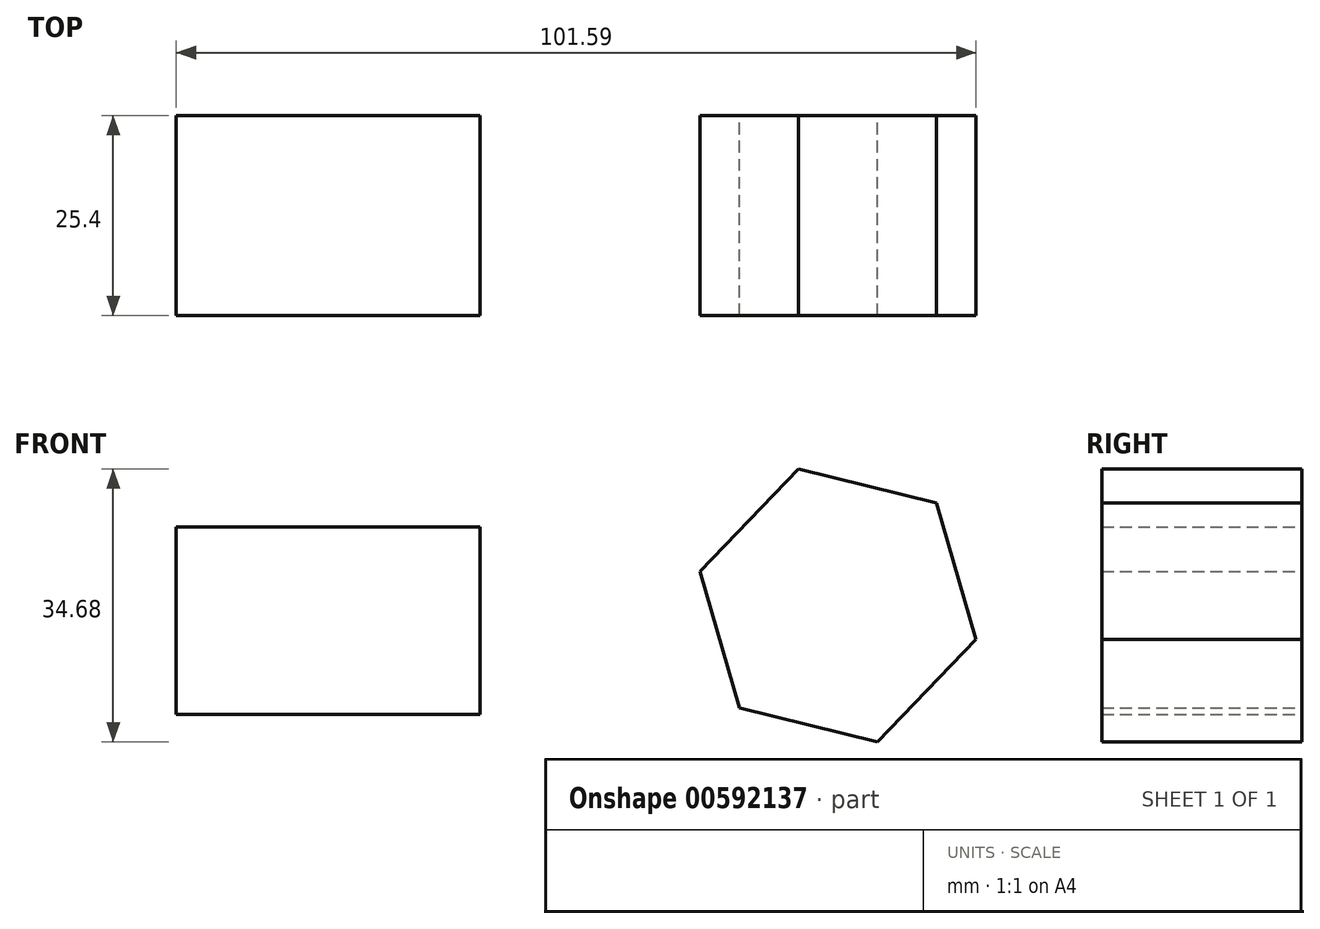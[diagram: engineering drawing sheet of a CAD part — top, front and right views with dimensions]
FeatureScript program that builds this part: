
annotation { "Feature Type Name" : "Feature", "Feature Type Description" : "" }
export const myFeature = defineFeature(function(context is Context, id is Id, definition is map)
    precondition{}
    {
        {
            var Q0;
            Q0=qCreatedBy(makeId("Front.planeOp"),FACE);
            var sketch = newSketch(context, id + "F0", { "sketchPlane" : qUnion([Q0])});
            skLineSegment(sketch, "E0.bottom", {"start": v(-62.62, 49.19) * mm, "end": v(-24.05, 49.19) * mm});
            skLineSegment(sketch, "E0.top", {"start": v(-62.62, 25.35) * mm, "end": v(-24.05, 25.35) * mm});
            skLineSegment(sketch, "E0.left", {"start": v(-62.62, 49.19) * mm, "end": v(-62.62, 25.35) * mm});
            skLineSegment(sketch, "E0.right", {"start": v(-24.05, 49.19) * mm, "end": v(-24.05, 25.35) * mm});
            skSolve(sketch);
        }
        {
            var Q0;
            Q0 = qSketchRegion(id + "F0", true);
            extrude(context, id + "F1", {"entities" : qUnion([Q0]), "depth" : 25.4 * mm, "offsetDistance" : 25.4 * mm});
        }
        {
            var Q0;
            Q0=qCreatedBy(makeId("Front.planeOp"),FACE);
            var sketch = newSketch(context, id + "F2", { "sketchPlane" : qUnion([Q0])});
            skCircle(sketch, "E1.cCircle", {"center": v(21.45, 39.22) * mm, "radius": 15.63 * mm, "construction": true});
            skLineSegment(sketch, "E1.0", {"start": v(38.97, 34.89) * mm, "end": v(26.46, 21.88) * mm});
            skLineSegment(sketch, "E1.1", {"start": v(26.46, 21.88) * mm, "end": v(8.94, 26.2) * mm});
            skLineSegment(sketch, "E1.2", {"start": v(8.94, 26.2) * mm, "end": v(3.93, 43.55) * mm});
            skLineSegment(sketch, "E1.3", {"start": v(3.93, 43.55) * mm, "end": v(16.44, 56.56) * mm});
            skLineSegment(sketch, "E1.4", {"start": v(16.44, 56.56) * mm, "end": v(33.96, 52.23) * mm});
            skLineSegment(sketch, "E1.5", {"start": v(33.96, 52.23) * mm, "end": v(38.97, 34.89) * mm});
            skPoint(sketch, "E1.0.midPoint", {"position": v(32.72, 28.38) * mm});
            skSolve(sketch);
        }
        {
            var Q0;
            Q0 = qSketchRegion(id + "F2", true);
            extrude(context, id + "F3", {"entities" : qUnion([Q0]), "depth" : 25.4 * mm, "offsetDistance" : 25.4 * mm});
        }
    });
